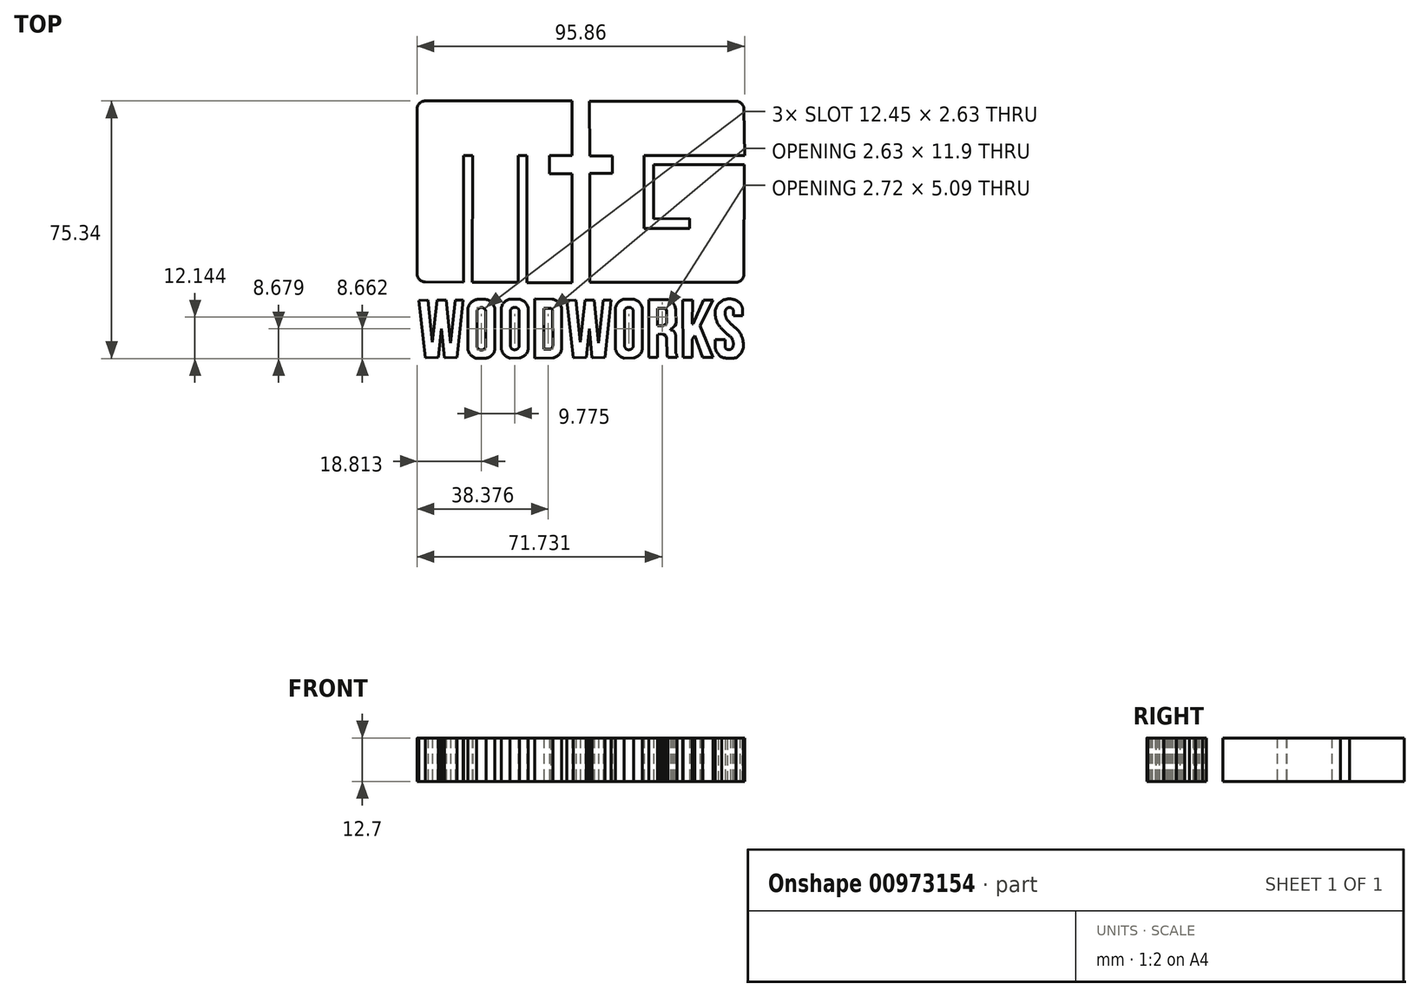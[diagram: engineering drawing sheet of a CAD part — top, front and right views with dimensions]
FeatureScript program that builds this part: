
annotation { "Feature Type Name" : "Feature", "Feature Type Description" : "" }
export const myFeature = defineFeature(function(context is Context, id is Id, definition is map)
    precondition{}
    {
        {
            var Q0;
            Q0=qCreatedBy(makeId("Top.planeOp"),FACE);
            var sketch = newSketch(context, id + "F0", { "sketchPlane" : qUnion([Q0])});
            skLineSegment(sketch, "E0", {"start": v(-2.56, 37.67) * mm, "end": v(-45.54, 37.67) * mm});
            skLineSegment(sketch, "E1", {"start": v(-47.93, 35.29) * mm, "end": v(-47.93, -12.9) * mm});
            skLineSegment(sketch, "E2", {"start": v(-45.58, -15.27) * mm, "end": v(-34.34, -15.42) * mm});
            skLineSegment(sketch, "E3", {"start": v(-34.34, -15.42) * mm, "end": v(-34.32, 21.71) * mm});
            skLineSegment(sketch, "E4", {"start": v(-34.32, 21.71) * mm, "end": v(-31.7, 21.71) * mm});
            skLineSegment(sketch, "E5", {"start": v(-31.7, 21.71) * mm, "end": v(-31.79, -15.4) * mm});
            skLineSegment(sketch, "E6", {"start": v(-31.79, -15.4) * mm, "end": v(-18.37, -15.4) * mm});
            skLineSegment(sketch, "E7", {"start": v(-18.37, -15.4) * mm, "end": v(-18.37, 21.74) * mm});
            skLineSegment(sketch, "E8", {"start": v(-18.37, 21.74) * mm, "end": v(-15.83, 21.74) * mm});
            skLineSegment(sketch, "E9", {"start": v(-15.83, 21.74) * mm, "end": v(-15.83, -15.5) * mm});
            skLineSegment(sketch, "E10", {"start": v(-15.83, -15.5) * mm, "end": v(-2.55, -15.5) * mm});
            skLineSegment(sketch, "E11", {"start": v(-2.55, -15.5) * mm, "end": v(-2.55, 16.43) * mm});
            skLineSegment(sketch, "E12", {"start": v(-2.55, 16.43) * mm, "end": v(-9.17, 16.43) * mm});
            skLineSegment(sketch, "E13", {"start": v(-9.17, 16.43) * mm, "end": v(-9.17, 21.7) * mm});
            skLineSegment(sketch, "E14", {"start": v(-9.17, 21.7) * mm, "end": v(-2.54, 21.7) * mm});
            skLineSegment(sketch, "E15", {"start": v(-2.54, 21.7) * mm, "end": v(-2.56, 37.67) * mm});
            skLineSegment(sketch, "E16", {"start": v(2.55, 37.6) * mm, "end": v(45.33, 37.63) * mm});
            skLineSegment(sketch, "E17", {"start": v(47.7, 35.3) * mm, "end": v(47.93, 21.69) * mm});
            skLineSegment(sketch, "E18", {"start": v(47.93, 21.69) * mm, "end": v(18.52, 21.69) * mm});
            skLineSegment(sketch, "E19", {"start": v(18.52, 21.69) * mm, "end": v(18.52, 0.4) * mm});
            skLineSegment(sketch, "E20", {"start": v(18.52, 0.4) * mm, "end": v(31.87, 0.4) * mm});
            skLineSegment(sketch, "E21", {"start": v(31.87, 0.4) * mm, "end": v(31.87, 3.23) * mm});
            skLineSegment(sketch, "E22", {"start": v(31.87, 3.23) * mm, "end": v(21.23, 3.15) * mm});
            skLineSegment(sketch, "E23", {"start": v(21.23, 3.15) * mm, "end": v(21.23, 19.01) * mm});
            skLineSegment(sketch, "E24", {"start": v(21.23, 19.01) * mm, "end": v(47.8, 19.01) * mm});
            skLineSegment(sketch, "E25", {"start": v(47.8, 19.01) * mm, "end": v(47.74, -13.03) * mm});
            skLineSegment(sketch, "E26", {"start": v(45.36, -15.4) * mm, "end": v(2.57, -15.4) * mm});
            skLineSegment(sketch, "E27", {"start": v(2.57, -15.4) * mm, "end": v(2.57, 16.45) * mm});
            skLineSegment(sketch, "E28", {"start": v(2.57, 16.45) * mm, "end": v(9.26, 16.5) * mm});
            skLineSegment(sketch, "E29", {"start": v(9.26, 16.5) * mm, "end": v(9.26, 21.64) * mm});
            skLineSegment(sketch, "E30", {"start": v(9.26, 21.64) * mm, "end": v(2.59, 21.64) * mm});
            skLineSegment(sketch, "E31", {"start": v(2.59, 21.64) * mm, "end": v(2.55, 37.6) * mm});
            skLineSegment(sketch, "E32", {"start": v(-47.43, -20.67) * mm, "end": v(-45.5, -37.42) * mm});
            skLineSegment(sketch, "E33", {"start": v(-45.5, -37.42) * mm, "end": v(-41.7, -37.35) * mm});
            skLineSegment(sketch, "E34", {"start": v(-41.7, -37.35) * mm, "end": v(-40.8, -29.01) * mm});
            skLineSegment(sketch, "E35", {"start": v(-40.8, -29.01) * mm, "end": v(-39.98, -37.42) * mm});
            skLineSegment(sketch, "E36", {"start": v(-39.98, -37.42) * mm, "end": v(-36.19, -37.35) * mm});
            skLineSegment(sketch, "E37", {"start": v(-36.19, -37.35) * mm, "end": v(-34.47, -20.6) * mm});
            skLineSegment(sketch, "E38", {"start": v(-34.47, -20.6) * mm, "end": v(-36.77, -20.58) * mm});
            skLineSegment(sketch, "E39", {"start": v(-36.77, -20.58) * mm, "end": v(-38.17, -33.2) * mm});
            skLineSegment(sketch, "E40", {"start": v(-38.17, -33.2) * mm, "end": v(-39.36, -20.58) * mm});
            skLineSegment(sketch, "E41", {"start": v(-39.36, -20.58) * mm, "end": v(-42.09, -20.58) * mm});
            skLineSegment(sketch, "E42", {"start": v(-42.09, -20.58) * mm, "end": v(-43.5, -32.97) * mm});
            skLineSegment(sketch, "E43", {"start": v(-43.5, -32.97) * mm, "end": v(-44.7, -20.64) * mm});
            skLineSegment(sketch, "E44", {"start": v(-44.7, -20.64) * mm, "end": v(-47.43, -20.67) * mm});
            skLineSegment(sketch, "E45", {"start": v(-33.1, -23.09) * mm, "end": v(-33.1, -34.98) * mm});
            skLineSegment(sketch, "E46", {"start": v(-30.43, -23.8) * mm, "end": v(-30.41, -34.05) * mm});
            skLineSegment(sketch, "E47", {"start": v(-27.83, -23.77) * mm, "end": v(-27.8, -34.01) * mm});
            skLineSegment(sketch, "E48", {"start": v(-25.15, -23.46) * mm, "end": v(-25.15, -34.62) * mm});
            skArc(sketch, "E49", {"start": v(-30.41, -34.05) * mm, "mid": v(-29.09, -35.22) * mm, "end": v(-27.8, -34.01) * mm});
            skArc(sketch, "E50", {"start": v(-33.1, -34.98) * mm, "mid": v(-32.19, -36.66) * mm, "end": v(-30.54, -37.63) * mm});
            skArc(sketch, "E51", {"start": v(-27.73, -37.6) * mm, "mid": v(-25.91, -36.57) * mm, "end": v(-25.15, -34.62) * mm});
            skLineSegment(sketch, "E52", {"start": v(-27.73, -37.6) * mm, "end": v(-30.54, -37.63) * mm});
            skArc(sketch, "E53", {"start": v(-27.83, -23.77) * mm, "mid": v(-29.15, -22.77) * mm, "end": v(-30.43, -23.8) * mm});
            skArc(sketch, "E54", {"start": v(-30.27, -20.35) * mm, "mid": v(-32.13, -21.26) * mm, "end": v(-33.1, -23.09) * mm});
            skArc(sketch, "E55", {"start": v(-25.15, -23.46) * mm, "mid": v(-25.98, -21.41) * mm, "end": v(-27.93, -20.37) * mm});
            skLineSegment(sketch, "E56", {"start": v(-27.93, -20.37) * mm, "end": v(-30.27, -20.35) * mm});
            skLineSegment(sketch, "E57", {"start": v(-23.33, -23) * mm, "end": v(-23.33, -34.9) * mm});
            skLineSegment(sketch, "E58", {"start": v(-20.66, -23.73) * mm, "end": v(-20.64, -33.97) * mm});
            skLineSegment(sketch, "E59", {"start": v(-18.06, -23.7) * mm, "end": v(-18.03, -33.94) * mm});
            skLineSegment(sketch, "E60", {"start": v(-15.37, -23.39) * mm, "end": v(-15.37, -34.55) * mm});
            skArc(sketch, "E61", {"start": v(-20.64, -33.97) * mm, "mid": v(-19.32, -35.14) * mm, "end": v(-18.03, -33.94) * mm});
            skArc(sketch, "E62", {"start": v(-23.33, -34.9) * mm, "mid": v(-22.41, -36.58) * mm, "end": v(-20.76, -37.55) * mm});
            skArc(sketch, "E63", {"start": v(-17.96, -37.53) * mm, "mid": v(-16.14, -36.5) * mm, "end": v(-15.37, -34.55) * mm});
            skLineSegment(sketch, "E64", {"start": v(-17.96, -37.53) * mm, "end": v(-20.76, -37.55) * mm});
            skArc(sketch, "E65", {"start": v(-18.06, -23.7) * mm, "mid": v(-19.37, -22.69) * mm, "end": v(-20.66, -23.73) * mm});
            skArc(sketch, "E66", {"start": v(-20.5, -20.27) * mm, "mid": v(-22.35, -21.19) * mm, "end": v(-23.33, -23) * mm});
            skArc(sketch, "E67", {"start": v(-15.37, -23.39) * mm, "mid": v(-16.2, -21.34) * mm, "end": v(-18.15, -20.3) * mm});
            skLineSegment(sketch, "E68", {"start": v(-18.15, -20.3) * mm, "end": v(-20.5, -20.27) * mm});
            skLineSegment(sketch, "E69", {"start": v(10.08, -23) * mm, "end": v(10.08, -34.9) * mm});
            skLineSegment(sketch, "E70", {"start": v(12.75, -23.73) * mm, "end": v(12.77, -33.97) * mm});
            skLineSegment(sketch, "E71", {"start": v(15.35, -23.7) * mm, "end": v(15.38, -33.94) * mm});
            skLineSegment(sketch, "E72", {"start": v(18.03, -23.39) * mm, "end": v(18.03, -34.55) * mm});
            skArc(sketch, "E73", {"start": v(12.77, -33.97) * mm, "mid": v(14.1, -35.14) * mm, "end": v(15.38, -33.94) * mm});
            skArc(sketch, "E74", {"start": v(10.08, -34.9) * mm, "mid": v(11, -36.58) * mm, "end": v(12.65, -37.55) * mm});
            skArc(sketch, "E75", {"start": v(15.45, -37.53) * mm, "mid": v(17.27, -36.5) * mm, "end": v(18.03, -34.55) * mm});
            skLineSegment(sketch, "E76", {"start": v(15.45, -37.53) * mm, "end": v(12.65, -37.55) * mm});
            skArc(sketch, "E77", {"start": v(15.35, -23.7) * mm, "mid": v(14.03, -22.69) * mm, "end": v(12.75, -23.73) * mm});
            skArc(sketch, "E78", {"start": v(12.91, -20.27) * mm, "mid": v(11.06, -21.19) * mm, "end": v(10.08, -23) * mm});
            skArc(sketch, "E79", {"start": v(18.03, -23.39) * mm, "mid": v(17.2, -21.34) * mm, "end": v(15.25, -20.3) * mm});
            skLineSegment(sketch, "E80", {"start": v(15.25, -20.3) * mm, "end": v(12.91, -20.27) * mm});
            skLineSegment(sketch, "E81", {"start": v(-4.16, -20.67) * mm, "end": v(-2.22, -37.42) * mm});
            skLineSegment(sketch, "E82", {"start": v(-2.22, -37.42) * mm, "end": v(1.58, -37.35) * mm});
            skLineSegment(sketch, "E83", {"start": v(1.58, -37.35) * mm, "end": v(2.47, -29.01) * mm});
            skLineSegment(sketch, "E84", {"start": v(2.47, -29.01) * mm, "end": v(3.29, -37.42) * mm});
            skLineSegment(sketch, "E85", {"start": v(3.29, -37.42) * mm, "end": v(7.09, -37.35) * mm});
            skLineSegment(sketch, "E86", {"start": v(7.09, -37.35) * mm, "end": v(8.8, -20.6) * mm});
            skLineSegment(sketch, "E87", {"start": v(8.8, -20.6) * mm, "end": v(6.5, -20.58) * mm});
            skLineSegment(sketch, "E88", {"start": v(6.5, -20.58) * mm, "end": v(5.1, -33.2) * mm});
            skLineSegment(sketch, "E89", {"start": v(5.1, -33.2) * mm, "end": v(3.9, -20.58) * mm});
            skLineSegment(sketch, "E90", {"start": v(3.9, -20.58) * mm, "end": v(1.18, -20.58) * mm});
            skLineSegment(sketch, "E91", {"start": v(1.18, -20.58) * mm, "end": v(-0.23, -32.97) * mm});
            skLineSegment(sketch, "E92", {"start": v(-0.23, -32.97) * mm, "end": v(-1.44, -20.64) * mm});
            skLineSegment(sketch, "E93", {"start": v(-1.44, -20.64) * mm, "end": v(-4.16, -20.67) * mm});
            skLineSegment(sketch, "E94", {"start": v(-13.54, -20.25) * mm, "end": v(-13.54, -37.57) * mm});
            skLineSegment(sketch, "E95", {"start": v(-10.87, -23.06) * mm, "end": v(-10.85, -34.96) * mm});
            skLineSegment(sketch, "E96", {"start": v(-8.27, -23.7) * mm, "end": v(-8.24, -33.94) * mm});
            skLineSegment(sketch, "E97", {"start": v(-5.59, -23.39) * mm, "end": v(-5.59, -34.55) * mm});
            skArc(sketch, "E98", {"start": v(-8.88, -34.96) * mm, "mid": v(-8.43, -34.52) * mm, "end": v(-8.24, -33.94) * mm});
            skArc(sketch, "E99", {"start": v(-8.17, -37.53) * mm, "mid": v(-6.35, -36.5) * mm, "end": v(-5.59, -34.55) * mm});
            skLineSegment(sketch, "E100", {"start": v(-8.17, -37.53) * mm, "end": v(-13.54, -37.57) * mm});
            skArc(sketch, "E101", {"start": v(-8.27, -23.7) * mm, "mid": v(-8.41, -23.35) * mm, "end": v(-8.64, -23.06) * mm});
            skArc(sketch, "E102", {"start": v(-5.59, -23.39) * mm, "mid": v(-6.42, -21.34) * mm, "end": v(-8.37, -20.3) * mm});
            skLineSegment(sketch, "E103", {"start": v(-8.37, -20.3) * mm, "end": v(-13.54, -20.25) * mm});
            skLineSegment(sketch, "E104", {"start": v(-8.64, -23.06) * mm, "end": v(-10.87, -23.06) * mm});
            skLineSegment(sketch, "E105", {"start": v(-8.88, -34.96) * mm, "end": v(-10.85, -34.96) * mm});
            skLineSegment(sketch, "E106", {"start": v(19.89, -37.34) * mm, "end": v(19.89, -20.52) * mm});
            skLineSegment(sketch, "E107", {"start": v(19.89, -20.52) * mm, "end": v(25.6, -20.52) * mm});
            skLineSegment(sketch, "E108", {"start": v(25.6, -20.52) * mm, "end": v(26.32, -20.96) * mm});
            skLineSegment(sketch, "E109", {"start": v(26.32, -20.96) * mm, "end": v(27, -21.54) * mm});
            skLineSegment(sketch, "E110", {"start": v(27, -21.54) * mm, "end": v(27.54, -22.25) * mm});
            skLineSegment(sketch, "E111", {"start": v(27.54, -22.25) * mm, "end": v(27.7, -22.85) * mm});
            skLineSegment(sketch, "E112", {"start": v(27.7, -22.85) * mm, "end": v(27.8, -23.3) * mm});
            skLineSegment(sketch, "E113", {"start": v(27.8, -23.3) * mm, "end": v(27.84, -27.4) * mm});
            skLineSegment(sketch, "E114", {"start": v(27.84, -27.4) * mm, "end": v(27.5, -28.1) * mm});
            skLineSegment(sketch, "E115", {"start": v(27.5, -28.1) * mm, "end": v(27.15, -28.47) * mm});
            skLineSegment(sketch, "E116", {"start": v(27.15, -28.47) * mm, "end": v(26.65, -28.94) * mm});
            skLineSegment(sketch, "E117", {"start": v(26.65, -28.94) * mm, "end": v(26.18, -29.13) * mm});
            skLineSegment(sketch, "E118", {"start": v(26.18, -29.13) * mm, "end": v(26.18, -29.36) * mm});
            skLineSegment(sketch, "E119", {"start": v(26.18, -29.36) * mm, "end": v(26.96, -29.5) * mm});
            skLineSegment(sketch, "E120", {"start": v(26.96, -29.5) * mm, "end": v(27.6, -30.24) * mm});
            skLineSegment(sketch, "E121", {"start": v(27.6, -30.24) * mm, "end": v(27.75, -31.15) * mm});
            skLineSegment(sketch, "E122", {"start": v(27.75, -31.15) * mm, "end": v(27.78, -36.19) * mm});
            skLineSegment(sketch, "E123", {"start": v(27.78, -36.19) * mm, "end": v(28.05, -36.4) * mm});
            skLineSegment(sketch, "E124", {"start": v(28.05, -36.4) * mm, "end": v(28.09, -37.35) * mm});
            skLineSegment(sketch, "E125", {"start": v(28.09, -37.35) * mm, "end": v(25.47, -37.32) * mm});
            skLineSegment(sketch, "E126", {"start": v(25.47, -37.32) * mm, "end": v(25.2, -36.75) * mm});
            skLineSegment(sketch, "E127", {"start": v(25.2, -36.75) * mm, "end": v(25.12, -31.73) * mm});
            skLineSegment(sketch, "E128", {"start": v(25.12, -31.73) * mm, "end": v(24.89, -30.97) * mm});
            skLineSegment(sketch, "E129", {"start": v(24.89, -30.97) * mm, "end": v(24.21, -30.56) * mm});
            skLineSegment(sketch, "E130", {"start": v(24.21, -30.56) * mm, "end": v(23.42, -30.45) * mm});
            skLineSegment(sketch, "E131", {"start": v(23.42, -30.45) * mm, "end": v(22.62, -30.6) * mm});
            skLineSegment(sketch, "E132", {"start": v(22.62, -30.6) * mm, "end": v(22.47, -30.86) * mm});
            skLineSegment(sketch, "E133", {"start": v(22.47, -30.86) * mm, "end": v(22.48, -37.35) * mm});
            skLineSegment(sketch, "E134", {"start": v(22.48, -37.35) * mm, "end": v(19.89, -37.34) * mm});
            skLineSegment(sketch, "E135", {"start": v(22.45, -28.03) * mm, "end": v(22.44, -22.98) * mm});
            skLineSegment(sketch, "E136", {"start": v(22.44, -22.98) * mm, "end": v(24.57, -23) * mm});
            skLineSegment(sketch, "E137", {"start": v(24.57, -23) * mm, "end": v(24.83, -23.18) * mm});
            skLineSegment(sketch, "E138", {"start": v(24.83, -23.18) * mm, "end": v(25.16, -23.73) * mm});
            skLineSegment(sketch, "E139", {"start": v(25.16, -23.73) * mm, "end": v(25.14, -27.12) * mm});
            skLineSegment(sketch, "E140", {"start": v(25.14, -27.12) * mm, "end": v(24.93, -27.52) * mm});
            skLineSegment(sketch, "E141", {"start": v(24.93, -27.52) * mm, "end": v(24.52, -27.88) * mm});
            skLineSegment(sketch, "E142", {"start": v(24.52, -27.88) * mm, "end": v(24.2, -28.07) * mm});
            skLineSegment(sketch, "E143", {"start": v(24.2, -28.07) * mm, "end": v(22.45, -28.03) * mm});
            skLineSegment(sketch, "E144", {"start": v(29.9, -37.38) * mm, "end": v(29.84, -20.56) * mm});
            skLineSegment(sketch, "E145", {"start": v(29.84, -20.56) * mm, "end": v(32.69, -20.54) * mm});
            skLineSegment(sketch, "E146", {"start": v(32.69, -20.54) * mm, "end": v(32.62, -27.53) * mm});
            skLineSegment(sketch, "E147", {"start": v(32.62, -27.53) * mm, "end": v(32.88, -27.53) * mm});
            skLineSegment(sketch, "E148", {"start": v(32.88, -27.53) * mm, "end": v(35.84, -20.59) * mm});
            skLineSegment(sketch, "E149", {"start": v(35.84, -20.59) * mm, "end": v(38.7, -20.57) * mm});
            skLineSegment(sketch, "E150", {"start": v(38.7, -20.57) * mm, "end": v(34.9, -28.08) * mm});
            skLineSegment(sketch, "E151", {"start": v(34.9, -28.08) * mm, "end": v(38.75, -37.35) * mm});
            skLineSegment(sketch, "E152", {"start": v(38.75, -37.35) * mm, "end": v(35.67, -37.37) * mm});
            skLineSegment(sketch, "E153", {"start": v(35.67, -37.37) * mm, "end": v(33.3, -31.04) * mm});
            skLineSegment(sketch, "E154", {"start": v(33.3, -31.04) * mm, "end": v(32.56, -32.07) * mm});
            skLineSegment(sketch, "E155", {"start": v(32.56, -32.07) * mm, "end": v(32.56, -37.36) * mm});
            skLineSegment(sketch, "E156", {"start": v(32.56, -37.36) * mm, "end": v(29.9, -37.38) * mm});
            skLineSegment(sketch, "E157", {"start": v(39.38, -34.68) * mm, "end": v(39.38, -32.2) * mm});
            skLineSegment(sketch, "E158", {"start": v(39.38, -32.2) * mm, "end": v(42.19, -32.2) * mm});
            skLineSegment(sketch, "E159", {"start": v(42.19, -32.2) * mm, "end": v(42.19, -34.45) * mm});
            skArc(sketch, "E160", {"start": v(42.19, -34.45) * mm, "mid": v(43.24, -35.1) * mm, "end": v(44.36, -34.59) * mm});
            skArc(sketch, "E161", {"start": v(44.36, -34.59) * mm, "mid": v(44.59, -32.88) * mm, "end": v(43.83, -31.33) * mm});
            skArc(sketch, "E162", {"start": v(40.37, -27.95) * mm, "mid": v(41.99, -29.75) * mm, "end": v(43.83, -31.33) * mm});
            skArc(sketch, "E163", {"start": v(39.3, -24.19) * mm, "mid": v(39.56, -26.15) * mm, "end": v(40.37, -27.95) * mm});
            skArc(sketch, "E164", {"start": v(42.2, -20.41) * mm, "mid": v(40.15, -21.83) * mm, "end": v(39.3, -24.19) * mm});
            skArc(sketch, "E165", {"start": v(46.54, -21.44) * mm, "mid": v(44.5, -20.35) * mm, "end": v(42.2, -20.41) * mm});
            skArc(sketch, "E166", {"start": v(47.37, -23.47) * mm, "mid": v(47.12, -22.39) * mm, "end": v(46.54, -21.44) * mm});
            skLineSegment(sketch, "E167", {"start": v(47.37, -23.47) * mm, "end": v(47.37, -25.16) * mm});
            skLineSegment(sketch, "E168", {"start": v(47.37, -25.16) * mm, "end": v(44.67, -25.17) * mm});
            skLineSegment(sketch, "E169", {"start": v(44.67, -25.17) * mm, "end": v(44.66, -23.57) * mm});
            skArc(sketch, "E170", {"start": v(44.66, -23.57) * mm, "mid": v(43.48, -22.75) * mm, "end": v(42.33, -23.62) * mm});
            skArc(sketch, "E171", {"start": v(42.33, -23.62) * mm, "mid": v(42.33, -25.18) * mm, "end": v(43.01, -26.58) * mm});
            skArc(sketch, "E172", {"start": v(43.01, -26.58) * mm, "mid": v(44.24, -27.86) * mm, "end": v(45.6, -28.99) * mm});
            skArc(sketch, "E173", {"start": v(47.47, -32.77) * mm, "mid": v(46.89, -30.7) * mm, "end": v(45.6, -28.99) * mm});
            skArc(sketch, "E174", {"start": v(45.36, -37.48) * mm, "mid": v(47.22, -35.49) * mm, "end": v(47.47, -32.77) * mm});
            skArc(sketch, "E175", {"start": v(41.22, -37.28) * mm, "mid": v(43.28, -37.66) * mm, "end": v(45.36, -37.48) * mm});
            skArc(sketch, "E176", {"start": v(39.38, -34.68) * mm, "mid": v(40.03, -36.18) * mm, "end": v(41.22, -37.28) * mm});
            skArc(sketch, "E177", {"start": v(-45.54, 37.67) * mm, "mid": v(-47.23, 36.97) * mm, "end": v(-47.93, 35.29) * mm});
            skArc(sketch, "E178", {"start": v(-47.93, -12.9) * mm, "mid": v(-47.24, -14.56) * mm, "end": v(-45.58, -15.27) * mm});
            skArc(sketch, "E179", {"start": v(45.36, -15.4) * mm, "mid": v(47.04, -14.71) * mm, "end": v(47.74, -13.03) * mm});
            skArc(sketch, "E180", {"start": v(47.7, 35.3) * mm, "mid": v(47, 36.95) * mm, "end": v(45.33, 37.63) * mm});
            skSolve(sketch);
        }
        {
            var Q0;
            Q0 = qSketchRegion(id + "F0", true);
            extrude(context, id + "F1", {"entities" : qUnion([Q0]), "depth" : 12.7 * mm, "offsetDistance" : 25.4 * mm});
        }
    });
